# Revit family: 306_d8aa2f75ffba4e099cb91f7eac2bbf
name_source: partatom
category: Pipe Accessories
units: mm (PartAtom-declared; Revit-internal decimal feet)

## family parameters
Always vertical = Yes
Cut with Voids When Loaded = No
Part Type = Valve - Breaks Into
Round Connector Dimension = Use Diameter
Shared = No
Work Plane-Based = No

## types (8) — shared parameters
CAT0 = Yes
Description = 3-way Fan coil valve VLG132, PN16 external thread
E = 16 mm  [stored 0.0524934 ft]
L2D = 38 mm  [stored 0.124672 ft]
L2D_Min = 3048 mm  [stored 10 ft]
MC = No
Manufacturer = ESBE
QmdConnectorList = 301;D;302;D
R10 = 8 mm  [stored 0.0262467 ft]
R7 = 15 mm  [stored 0.0492126 ft]
R8 = 2 mm  [stored 0.00656168 ft]
R9 = 9 mm  [stored 0.0295276 ft]
URL = http://www.esbe.eu
W2D = 15 mm  [stored 0.0492126 ft]
X4 = 7 mm  [stored 0.0229659 ft]
X4__ve = -7 mm  [stored -0.0229659 ft]
Z3 = 2 mm  [stored 0.00656168 ft]
Z5 = 9 mm  [stored 0.0295276 ft]
Z7 = 3 mm  [stored 0.00984252 ft]
Z7__ve = -3 mm
Z8 = 4 mm  [stored 0.0131234 ft]
magiPartTypeId = 306
magiProductFamilyId = d8aa2f75ffba4e099cb91f7eac2bbf

## per-type parameters (varying)
| type | C | D | DT2 | H | H1 | LT2 | MC Product Code | R1 | R2 | R6 | X3 | Z1 | Z2 | Z9 | magiProductId |
| VLG132 PN16 15-0,25 G1/2 | 25 mm  [stored 0.082021 ft] | 15 mm | 8 mm  [stored 0.0262467 ft] | 27 mm | 24 mm | 19 mm  [stored 0.062336 ft] | VLG132 PN16 15-0,25 G1/2" | 7 mm  [stored 0.0229659 ft] | 13 mm | 9 mm  [stored 0.0295276 ft] | 34 mm  [stored 0.111549 ft] | 4 mm  [stored 0.0131234 ft] | 5 mm  [stored 0.0164042 ft] | 7 mm  [stored 0.0229659 ft] | 9731506c0340485ea4b362512447dd |
| VLG132 PN16 15-0,4 G1/2 | 25 mm  [stored 0.082021 ft] | 15 mm | 8 mm  [stored 0.0262467 ft] | 27 mm | 24 mm | 19 mm  [stored 0.062336 ft] | VLG132 PN16 15-0,4 G1/2" | 7 mm  [stored 0.0229659 ft] | 13 mm | 9 mm  [stored 0.0295276 ft] | 34 mm  [stored 0.111549 ft] | 4 mm  [stored 0.0131234 ft] | 5 mm  [stored 0.0164042 ft] | 7 mm  [stored 0.0229659 ft] | 6f9dee4389ea4e3d87beb0e9792f91 |
| VLG132 PN16 15-0,6 G1/2 | 25 mm  [stored 0.082021 ft] | 15 mm | 8 mm  [stored 0.0262467 ft] | 27 mm | 24 mm | 19 mm  [stored 0.062336 ft] | VLG132 PN16 15-0,6 G1/2" | 7 mm  [stored 0.0229659 ft] | 13 mm | 9 mm  [stored 0.0295276 ft] | 34 mm  [stored 0.111549 ft] | 4 mm  [stored 0.0131234 ft] | 5 mm  [stored 0.0164042 ft] | 7 mm  [stored 0.0229659 ft] | 96f79241b0ae41e08777c5d0260a0f |
| VLG132 PN16 15-1,0 G1/2 | 25 mm  [stored 0.082021 ft] | 15 mm | 8 mm  [stored 0.0262467 ft] | 27 mm | 24 mm | 19 mm  [stored 0.062336 ft] | VLG132 PN16 15-1,0 G1/2" | 7 mm  [stored 0.0229659 ft] | 13 mm | 9 mm  [stored 0.0295276 ft] | 34 mm  [stored 0.111549 ft] | 4 mm  [stored 0.0131234 ft] | 5 mm  [stored 0.0164042 ft] | 7 mm  [stored 0.0229659 ft] | b0a924e432774a1799cb0bb70b03fe |
| VLG132 PN16 15-1,6 G1/2 | 25 mm  [stored 0.082021 ft] | 15 mm | 8 mm  [stored 0.0262467 ft] | 27 mm | 24 mm | 19 mm  [stored 0.062336 ft] | VLG132 PN16 15-1,6 G1/2" | 7 mm  [stored 0.0229659 ft] | 13 mm | 9 mm  [stored 0.0295276 ft] | 34 mm  [stored 0.111549 ft] | 4 mm  [stored 0.0131234 ft] | 5 mm  [stored 0.0164042 ft] | 7 mm  [stored 0.0229659 ft] | e97539bc73ed4baeb6190fba2b64e6 |
| VLG132 PN16 20-2,5 G3/4 | 34 mm  [stored 0.111549 ft] | 20 mm | 10 mm  [stored 0.0328084 ft] | 26 mm | 29 mm  [stored 0.0951444 ft] | 21 mm  [stored 0.0688976 ft] | VLG132 PN16 20-2,5 G3/4" | 9 mm  [stored 0.0295276 ft] | 15 mm  [stored 0.0492126 ft] | 12 mm  [stored 0.0393701 ft] | 38 mm  [stored 0.124672 ft] | 5 mm  [stored 0.0164042 ft] | 7 mm  [stored 0.0229659 ft] | 9 mm  [stored 0.0295276 ft] | 741f6f2fd14b4b9a85de3866386587 |
| VLG132 PN16 20-4,0 G3/4 | 34 mm  [stored 0.111549 ft] | 20 mm | 10 mm  [stored 0.0328084 ft] | 26 mm | 29 mm  [stored 0.0951444 ft] | 21 mm  [stored 0.0688976 ft] | VLG132 PN16 20-4,0 G3/4" | 9 mm  [stored 0.0295276 ft] | 15 mm  [stored 0.0492126 ft] | 12 mm  [stored 0.0393701 ft] | 38 mm  [stored 0.124672 ft] | 5 mm  [stored 0.0164042 ft] | 7 mm  [stored 0.0229659 ft] | 9 mm  [stored 0.0295276 ft] | 50ed762ffd2a44fcadf6881736ff13 |
| VLG132 PN16 20-6,0 G3/4 | 34 mm  [stored 0.111549 ft] | 20 mm | 10 mm  [stored 0.0328084 ft] | 26 mm | 29 mm  [stored 0.0951444 ft] | 21 mm  [stored 0.0688976 ft] | VLG132 PN16 20-6,0 G3/4" | 9 mm  [stored 0.0295276 ft] | 15 mm  [stored 0.0492126 ft] | 12 mm  [stored 0.0393701 ft] | 38 mm  [stored 0.124672 ft] | 5 mm  [stored 0.0164042 ft] | 7 mm  [stored 0.0229659 ft] | 9 mm  [stored 0.0295276 ft] | f0f349b6853447d69be1556958a504 |

note: [stored X ft] marks values corroborated as IEEE doubles in the binary element streams (Revit-internal decimal feet)

## geometry (parser evidence)
native form markers: Sweep x3
no freeform markers — native parametric forms only
